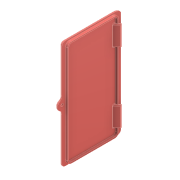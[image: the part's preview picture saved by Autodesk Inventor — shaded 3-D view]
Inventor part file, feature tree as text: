
AUTODESK INVENTOR PART (.ipt)
format: ipt  version: 2021 (Build 250183000, 183)  size: 358,912 bytes
history: native  units: mm
features: projected_geometry x3, chamfer x2, extrude x1, fillet x1, sketch x1
ambient origin geometry x8: Origin, YZ Plane, XZ Plane, XY Plane, X Axis, Y Axis, Z Axis, Center Point
bodies: Volumenkörper1 (feature_tree), Body1 (feature_tree)
feature tree (8):
  extrude  "Extrusion1"  Depth=1.0mm TaperAngle=45.0deg
  chamfer  "Fase1"  Distance=1.2mm
  fillet  "Rundung1"  Radius=1.0mm
  chamfer  "Fase2"  [1 undecoded]
  sketch  "Skizze1"  dims[d0=0.8mm d1=0.0mm d2=1.8mm d3=2.0mm d4=45.0deg d5=1.2mm d6=1.0mm d7=2.0mm d8=45.0deg]
  projected_geometry  "Projizierte Kontur1"
  projected_geometry  "Projizierte Kontur2"
  projected_geometry  "Projizierte Kontur3"
note: 1 required parameter value undecoded (feature->parameter linkage not recoverable at this tier; creation-order binding heuristic only, values carry confidence <= 0.55)
